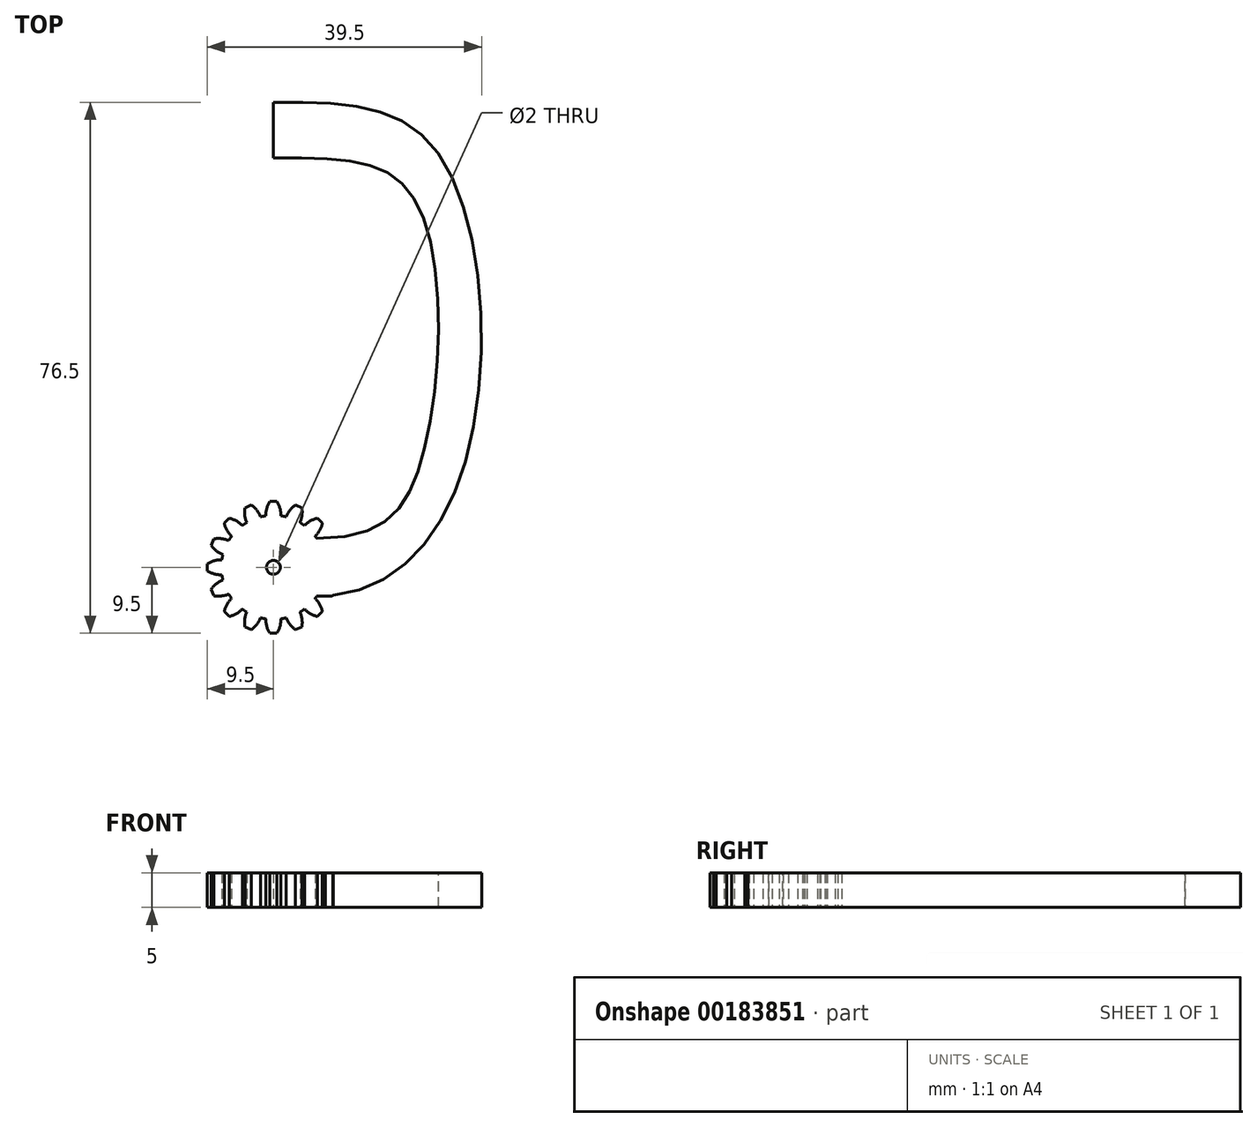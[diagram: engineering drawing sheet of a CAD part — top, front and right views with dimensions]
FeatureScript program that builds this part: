
annotation { "Feature Type Name" : "Feature", "Feature Type Description" : "" }
export const myFeature = defineFeature(function(context is Context, id is Id, definition is map)
    precondition{}
    {
        {
            var Q0;
            Q0=qCreatedBy(makeId("Top.planeOp"),FACE);
            var sketch = newSketch(context, id + "F0", { "sketchPlane" : qUnion([Q0])});
            skCircle(sketch, "E0", {"center": v(0, 0) * mm, "radius": 7.5 * mm});
            skLineSegment(sketch, "E1", {"start": v(0, 0) * mm, "end": v(0, 7.5) * mm, "construction": true});
            skLineSegment(sketch, "E2", {"start": v(0, 7.5) * mm, "end": v(0, 9.5) * mm});
            skLineSegment(sketch, "E3", {"start": v(0, 9.5) * mm, "end": v(-0.5, 9.5) * mm});
            skArc(sketch, "E4", {"start": v(-0.5, 9.5) * mm, "mid": v(-0.95, 8.5) * mm, "end": v(-1.09, 7.42) * mm});
            skLineSegment(sketch, "E5.MirrorCS", {"start": v(0, 9.5) * mm, "end": v(0.5, 9.5) * mm});
            skArc(sketch, "E6.MirrorCS", {"start": v(0.5, 9.5) * mm, "mid": v(0.95, 8.5) * mm, "end": v(1.09, 7.42) * mm});
            skArc(sketch, "E7.1.0", {"start": v(-4.1, 8.59) * mm, "mid": v(-4.13, 7.5) * mm, "end": v(-3.85, 6.44) * mm});
            skLineSegment(sketch, "E7.1.1", {"start": v(-3.64, 8.78) * mm, "end": v(-4.1, 8.59) * mm});
            skLineSegment(sketch, "E7.1.2", {"start": v(-3.64, 8.78) * mm, "end": v(-3.17, 8.97) * mm});
            skArc(sketch, "E7.1.3", {"start": v(-3.17, 8.97) * mm, "mid": v(-2.38, 8.22) * mm, "end": v(-1.83, 7.27) * mm});
            skArc(sketch, "E7.2.0", {"start": v(-7.07, 6.36) * mm, "mid": v(-6.69, 5.34) * mm, "end": v(-6.02, 4.48) * mm});
            skLineSegment(sketch, "E7.2.1", {"start": v(-6.72, 6.72) * mm, "end": v(-7.07, 6.36) * mm});
            skLineSegment(sketch, "E7.2.2", {"start": v(-6.72, 6.72) * mm, "end": v(-6.36, 7.07) * mm});
            skArc(sketch, "E7.2.3", {"start": v(-6.36, 7.07) * mm, "mid": v(-5.34, 6.69) * mm, "end": v(-4.48, 6.02) * mm});
            skArc(sketch, "E7.3.0", {"start": v(-8.97, 3.17) * mm, "mid": v(-8.22, 2.38) * mm, "end": v(-7.27, 1.83) * mm});
            skLineSegment(sketch, "E7.3.1", {"start": v(-8.78, 3.64) * mm, "end": v(-8.97, 3.17) * mm});
            skLineSegment(sketch, "E7.3.2", {"start": v(-8.78, 3.64) * mm, "end": v(-8.59, 4.1) * mm});
            skArc(sketch, "E7.3.3", {"start": v(-8.59, 4.1) * mm, "mid": v(-7.5, 4.13) * mm, "end": v(-6.44, 3.85) * mm});
            skArc(sketch, "E7.4.0", {"start": v(-9.5, -0.5) * mm, "mid": v(-8.5, -0.95) * mm, "end": v(-7.42, -1.09) * mm});
            skLineSegment(sketch, "E7.4.1", {"start": v(-9.5, 0) * mm, "end": v(-9.5, -0.5) * mm});
            skLineSegment(sketch, "E7.4.2", {"start": v(-9.5, 0) * mm, "end": v(-9.5, 0.5) * mm});
            skArc(sketch, "E7.4.3", {"start": v(-9.5, 0.5) * mm, "mid": v(-8.5, 0.95) * mm, "end": v(-7.42, 1.09) * mm});
            skArc(sketch, "E7.5.0", {"start": v(-8.59, -4.1) * mm, "mid": v(-7.5, -4.13) * mm, "end": v(-6.44, -3.85) * mm});
            skLineSegment(sketch, "E7.5.1", {"start": v(-8.78, -3.64) * mm, "end": v(-8.59, -4.1) * mm});
            skLineSegment(sketch, "E7.5.2", {"start": v(-8.78, -3.64) * mm, "end": v(-8.97, -3.17) * mm});
            skArc(sketch, "E7.5.3", {"start": v(-8.97, -3.17) * mm, "mid": v(-8.22, -2.38) * mm, "end": v(-7.27, -1.83) * mm});
            skArc(sketch, "E7.6.0", {"start": v(-6.36, -7.07) * mm, "mid": v(-5.34, -6.69) * mm, "end": v(-4.48, -6.02) * mm});
            skLineSegment(sketch, "E7.6.1", {"start": v(-6.72, -6.72) * mm, "end": v(-6.36, -7.07) * mm});
            skLineSegment(sketch, "E7.6.2", {"start": v(-6.72, -6.72) * mm, "end": v(-7.07, -6.36) * mm});
            skArc(sketch, "E7.6.3", {"start": v(-7.07, -6.36) * mm, "mid": v(-6.69, -5.34) * mm, "end": v(-6.02, -4.48) * mm});
            skArc(sketch, "E7.7.0", {"start": v(-3.17, -8.97) * mm, "mid": v(-2.38, -8.22) * mm, "end": v(-1.83, -7.27) * mm});
            skLineSegment(sketch, "E7.7.1", {"start": v(-3.64, -8.78) * mm, "end": v(-3.17, -8.97) * mm});
            skLineSegment(sketch, "E7.7.2", {"start": v(-3.64, -8.78) * mm, "end": v(-4.1, -8.59) * mm});
            skArc(sketch, "E7.7.3", {"start": v(-4.1, -8.59) * mm, "mid": v(-4.13, -7.5) * mm, "end": v(-3.85, -6.44) * mm});
            skArc(sketch, "E7.8.0", {"start": v(0.5, -9.5) * mm, "mid": v(0.95, -8.5) * mm, "end": v(1.09, -7.42) * mm});
            skLineSegment(sketch, "E7.8.1", {"start": v(0, -9.5) * mm, "end": v(0.5, -9.5) * mm});
            skLineSegment(sketch, "E7.8.2", {"start": v(0, -9.5) * mm, "end": v(-0.5, -9.5) * mm});
            skArc(sketch, "E7.8.3", {"start": v(-0.5, -9.5) * mm, "mid": v(-0.95, -8.5) * mm, "end": v(-1.09, -7.42) * mm});
            skArc(sketch, "E7.9.0", {"start": v(4.1, -8.59) * mm, "mid": v(4.13, -7.5) * mm, "end": v(3.85, -6.44) * mm});
            skLineSegment(sketch, "E7.9.1", {"start": v(3.64, -8.78) * mm, "end": v(4.1, -8.59) * mm});
            skLineSegment(sketch, "E7.9.2", {"start": v(3.64, -8.78) * mm, "end": v(3.17, -8.97) * mm});
            skArc(sketch, "E7.9.3", {"start": v(3.17, -8.97) * mm, "mid": v(2.38, -8.22) * mm, "end": v(1.83, -7.27) * mm});
            skArc(sketch, "E7.10.0", {"start": v(7.07, -6.36) * mm, "mid": v(6.69, -5.34) * mm, "end": v(6.02, -4.48) * mm});
            skLineSegment(sketch, "E7.10.1", {"start": v(6.72, -6.72) * mm, "end": v(7.07, -6.36) * mm});
            skLineSegment(sketch, "E7.10.2", {"start": v(6.72, -6.72) * mm, "end": v(6.36, -7.07) * mm});
            skArc(sketch, "E7.10.3", {"start": v(6.36, -7.07) * mm, "mid": v(5.34, -6.69) * mm, "end": v(4.48, -6.02) * mm});
            skArc(sketch, "E7.11.0", {"start": v(8.97, -3.17) * mm, "mid": v(8.22, -2.38) * mm, "end": v(7.27, -1.83) * mm});
            skLineSegment(sketch, "E7.11.1", {"start": v(8.78, -3.64) * mm, "end": v(8.97, -3.17) * mm});
            skLineSegment(sketch, "E7.11.2", {"start": v(8.78, -3.64) * mm, "end": v(8.59, -4.1) * mm});
            skArc(sketch, "E7.11.3", {"start": v(8.59, -4.1) * mm, "mid": v(7.5, -4.13) * mm, "end": v(6.44, -3.85) * mm});
            skArc(sketch, "E7.12.0", {"start": v(9.5, 0.5) * mm, "mid": v(8.5, 0.95) * mm, "end": v(7.42, 1.09) * mm});
            skLineSegment(sketch, "E7.12.1", {"start": v(9.5, 0) * mm, "end": v(9.5, 0.5) * mm});
            skLineSegment(sketch, "E7.12.2", {"start": v(9.5, 0) * mm, "end": v(9.5, -0.5) * mm});
            skArc(sketch, "E7.12.3", {"start": v(9.5, -0.5) * mm, "mid": v(8.5, -0.95) * mm, "end": v(7.42, -1.09) * mm});
            skArc(sketch, "E7.13.0", {"start": v(8.59, 4.1) * mm, "mid": v(7.5, 4.13) * mm, "end": v(6.44, 3.85) * mm});
            skLineSegment(sketch, "E7.13.1", {"start": v(8.78, 3.64) * mm, "end": v(8.59, 4.1) * mm});
            skLineSegment(sketch, "E7.13.2", {"start": v(8.78, 3.64) * mm, "end": v(8.97, 3.17) * mm});
            skArc(sketch, "E7.13.3", {"start": v(8.97, 3.17) * mm, "mid": v(8.22, 2.38) * mm, "end": v(7.27, 1.83) * mm});
            skArc(sketch, "E7.14.0", {"start": v(6.36, 7.07) * mm, "mid": v(5.34, 6.69) * mm, "end": v(4.48, 6.02) * mm});
            skLineSegment(sketch, "E7.14.1", {"start": v(6.72, 6.72) * mm, "end": v(6.36, 7.07) * mm});
            skLineSegment(sketch, "E7.14.2", {"start": v(6.72, 6.72) * mm, "end": v(7.07, 6.36) * mm});
            skArc(sketch, "E7.14.3", {"start": v(7.07, 6.36) * mm, "mid": v(6.69, 5.34) * mm, "end": v(6.02, 4.48) * mm});
            skArc(sketch, "E7.15.0", {"start": v(3.17, 8.97) * mm, "mid": v(2.38, 8.22) * mm, "end": v(1.83, 7.27) * mm});
            skLineSegment(sketch, "E7.15.1", {"start": v(3.64, 8.78) * mm, "end": v(3.17, 8.97) * mm});
            skLineSegment(sketch, "E7.15.2", {"start": v(3.64, 8.78) * mm, "end": v(4.1, 8.59) * mm});
            skArc(sketch, "E7.15.3", {"start": v(4.1, 8.59) * mm, "mid": v(4.13, 7.5) * mm, "end": v(3.85, 6.44) * mm});
            skSolve(sketch);
        }
        {
            var Q0;
            {var subQ0=sQuery(id+"F0.wireOp",EDGE,"E0");var subQ27=makeQuery(id+"F0.imprint","INTERSECT",VERTEX,{"derivedFrom":[subQ0,sQuery(id+"F0.wireOp",EDGE,"E7.12.0")]});Q0=makeQuery(id+"F0.imprint","IMPRINT",FACE,{"disambiguationData":[TD([[makeQuery(id+"F0.imprint","IMPRINT",EDGE,{"disambiguationData":[TD([[subQ27,-1.0]])],"derivedFrom":subQ0}),1.0]])]});}
            var Q1;
            {var subQ0=sQuery(id+"F0.wireOp",EDGE,"E7.8.0");Q1=makeQuery(id+"F0.imprint","IMPRINT",FACE,{"disambiguationData":[TD([[makeQuery(id+"F0.imprint","IMPRINT",EDGE,{"derivedFrom":subQ0}),1.0]])]});}
            var Q2;
            {var subQ0=sQuery(id+"F0.wireOp",EDGE,"E7.9.0");Q2=makeQuery(id+"F0.imprint","IMPRINT",FACE,{"disambiguationData":[TD([[makeQuery(id+"F0.imprint","IMPRINT",EDGE,{"derivedFrom":subQ0}),1.0]])]});}
            var Q3;
            {var subQ0=sQuery(id+"F0.wireOp",EDGE,"E7.11.0");Q3=makeQuery(id+"F0.imprint","IMPRINT",FACE,{"disambiguationData":[TD([[makeQuery(id+"F0.imprint","IMPRINT",EDGE,{"derivedFrom":subQ0}),1.0]])]});}
            var Q4;
            {var subQ0=sQuery(id+"F0.wireOp",EDGE,"E7.12.0");Q4=makeQuery(id+"F0.imprint","IMPRINT",FACE,{"disambiguationData":[TD([[makeQuery(id+"F0.imprint","IMPRINT",EDGE,{"derivedFrom":subQ0}),1.0]])]});}
            var Q5;
            {var subQ0=sQuery(id+"F0.wireOp",EDGE,"E7.10.0");Q5=makeQuery(id+"F0.imprint","IMPRINT",FACE,{"disambiguationData":[TD([[makeQuery(id+"F0.imprint","IMPRINT",EDGE,{"derivedFrom":subQ0}),1.0]])]});}
            var Q6;
            {var subQ0=sQuery(id+"F0.wireOp",EDGE,"E7.13.0");Q6=makeQuery(id+"F0.imprint","IMPRINT",FACE,{"disambiguationData":[TD([[makeQuery(id+"F0.imprint","IMPRINT",EDGE,{"derivedFrom":subQ0}),1.0]])]});}
            var Q7;
            {var subQ0=sQuery(id+"F0.wireOp",EDGE,"E7.14.0");Q7=makeQuery(id+"F0.imprint","IMPRINT",FACE,{"disambiguationData":[TD([[makeQuery(id+"F0.imprint","IMPRINT",EDGE,{"derivedFrom":subQ0}),1.0]])]});}
            var Q8;
            {var subQ0=sQuery(id+"F0.wireOp",EDGE,"E7.15.0");Q8=makeQuery(id+"F0.imprint","IMPRINT",FACE,{"disambiguationData":[TD([[makeQuery(id+"F0.imprint","IMPRINT",EDGE,{"derivedFrom":subQ0}),1.0]])]});}
            var Q9;
            {var subQ0=sQuery(id+"F0.wireOp",EDGE,"E7.7.0");Q9=makeQuery(id+"F0.imprint","IMPRINT",FACE,{"disambiguationData":[TD([[makeQuery(id+"F0.imprint","IMPRINT",EDGE,{"derivedFrom":subQ0}),1.0]])]});}
            var Q10;
            {var subQ0=sQuery(id+"F0.wireOp",EDGE,"E7.6.0");Q10=makeQuery(id+"F0.imprint","IMPRINT",FACE,{"disambiguationData":[TD([[makeQuery(id+"F0.imprint","IMPRINT",EDGE,{"derivedFrom":subQ0}),1.0]])]});}
            var Q11;
            {var subQ0=sQuery(id+"F0.wireOp",EDGE,"E7.5.0");Q11=makeQuery(id+"F0.imprint","IMPRINT",FACE,{"disambiguationData":[TD([[makeQuery(id+"F0.imprint","IMPRINT",EDGE,{"derivedFrom":subQ0}),1.0]])]});}
            var Q12;
            {var subQ1=sQuery(id+"F0.wireOp",EDGE,"E7.4.0");Q12=makeQuery(id+"F0.imprint","IMPRINT",FACE,{"disambiguationData":[TD([[makeQuery(id+"F0.imprint","IMPRINT",EDGE,{"derivedFrom":subQ1}),1.0]])]});}
            var Q13;
            {var subQ0=sQuery(id+"F0.wireOp",EDGE,"E7.3.0");Q13=makeQuery(id+"F0.imprint","IMPRINT",FACE,{"disambiguationData":[TD([[makeQuery(id+"F0.imprint","IMPRINT",EDGE,{"derivedFrom":subQ0}),1.0]])]});}
            var Q14;
            {var subQ0=sQuery(id+"F0.wireOp",EDGE,"E7.2.0");Q14=makeQuery(id+"F0.imprint","IMPRINT",FACE,{"disambiguationData":[TD([[makeQuery(id+"F0.imprint","IMPRINT",EDGE,{"derivedFrom":subQ0}),1.0]])]});}
            var Q15;
            {var subQ0=sQuery(id+"F0.wireOp",EDGE,"E7.1.0");Q15=makeQuery(id+"F0.imprint","IMPRINT",FACE,{"disambiguationData":[TD([[makeQuery(id+"F0.imprint","IMPRINT",EDGE,{"derivedFrom":subQ0}),1.0]])]});}
            var Q16;
            {var subQ0=sQuery(id+"F0.wireOp",EDGE,"E2");Q16=makeQuery(id+"F0.imprint","IMPRINT",FACE,{"disambiguationData":[TD([[makeQuery(id+"F0.imprint","IMPRINT",EDGE,{"derivedFrom":subQ0}),1.0]])]});}
            var Q17;
            {var subQ0=sQuery(id+"F0.wireOp",EDGE,"E2");Q17=makeQuery(id+"F0.imprint","IMPRINT",FACE,{"disambiguationData":[TD([[makeQuery(id+"F0.imprint","IMPRINT",EDGE,{"derivedFrom":subQ0}),-1.0]])]});}
            extrude(context, id + "F1", {"entities" : qUnion([Q0, Q1, Q2, Q3, Q4, Q5, Q6, Q7, Q8, Q9, Q10, Q11, Q12, Q13, Q14, Q15, Q16, Q17]), "depth" : 5 * mm});
        }
        {
            var Q0;
            Q0=makeQuery(id+"F1.opExtrude","CAP_FACE",FACE,{"disambiguationData":[OSD([sQuery(id+"F0.wireOp",EDGE,"E0"),sQuery(id+"F0.wireOp",EDGE,"E3"),sQuery(id+"F0.wireOp",EDGE,"E4"),sQuery(id+"F0.wireOp",EDGE,"E5.MirrorCS"),sQuery(id+"F0.wireOp",EDGE,"E6.MirrorCS"),sQuery(id+"F0.wireOp",EDGE,"E7.1.0"),sQuery(id+"F0.wireOp",EDGE,"E7.1.1"),sQuery(id+"F0.wireOp",EDGE,"E7.1.2"),sQuery(id+"F0.wireOp",EDGE,"E7.1.3"),sQuery(id+"F0.wireOp",EDGE,"E7.2.0"),sQuery(id+"F0.wireOp",EDGE,"E7.2.1"),sQuery(id+"F0.wireOp",EDGE,"E7.2.2"),sQuery(id+"F0.wireOp",EDGE,"E7.2.3"),sQuery(id+"F0.wireOp",EDGE,"E7.3.0"),sQuery(id+"F0.wireOp",EDGE,"E7.3.1"),sQuery(id+"F0.wireOp",EDGE,"E7.3.2"),sQuery(id+"F0.wireOp",EDGE,"E7.3.3"),sQuery(id+"F0.wireOp",EDGE,"E7.4.0"),sQuery(id+"F0.wireOp",EDGE,"E7.4.1"),sQuery(id+"F0.wireOp",EDGE,"E7.4.2"),sQuery(id+"F0.wireOp",EDGE,"E7.4.3"),sQuery(id+"F0.wireOp",EDGE,"E7.5.0"),sQuery(id+"F0.wireOp",EDGE,"E7.5.1"),sQuery(id+"F0.wireOp",EDGE,"E7.5.2"),sQuery(id+"F0.wireOp",EDGE,"E7.5.3"),sQuery(id+"F0.wireOp",EDGE,"E7.6.0"),sQuery(id+"F0.wireOp",EDGE,"E7.6.1"),sQuery(id+"F0.wireOp",EDGE,"E7.6.2"),sQuery(id+"F0.wireOp",EDGE,"E7.6.3"),sQuery(id+"F0.wireOp",EDGE,"E7.7.0"),sQuery(id+"F0.wireOp",EDGE,"E7.7.1"),sQuery(id+"F0.wireOp",EDGE,"E7.7.2"),sQuery(id+"F0.wireOp",EDGE,"E7.7.3"),sQuery(id+"F0.wireOp",EDGE,"E7.8.0"),sQuery(id+"F0.wireOp",EDGE,"E7.8.1"),sQuery(id+"F0.wireOp",EDGE,"E7.8.2"),sQuery(id+"F0.wireOp",EDGE,"E7.8.3"),sQuery(id+"F0.wireOp",EDGE,"E7.9.0"),sQuery(id+"F0.wireOp",EDGE,"E7.9.1"),sQuery(id+"F0.wireOp",EDGE,"E7.9.2"),sQuery(id+"F0.wireOp",EDGE,"E7.9.3"),sQuery(id+"F0.wireOp",EDGE,"E7.10.0"),sQuery(id+"F0.wireOp",EDGE,"E7.10.1"),sQuery(id+"F0.wireOp",EDGE,"E7.10.2"),sQuery(id+"F0.wireOp",EDGE,"E7.10.3"),sQuery(id+"F0.wireOp",EDGE,"E7.11.0"),sQuery(id+"F0.wireOp",EDGE,"E7.11.1"),sQuery(id+"F0.wireOp",EDGE,"E7.11.2"),sQuery(id+"F0.wireOp",EDGE,"E7.11.3"),sQuery(id+"F0.wireOp",EDGE,"E7.12.0"),sQuery(id+"F0.wireOp",EDGE,"E7.12.1"),sQuery(id+"F0.wireOp",EDGE,"E7.12.2"),sQuery(id+"F0.wireOp",EDGE,"E7.12.3"),sQuery(id+"F0.wireOp",EDGE,"E7.13.0"),sQuery(id+"F0.wireOp",EDGE,"E7.13.1"),sQuery(id+"F0.wireOp",EDGE,"E7.13.2"),sQuery(id+"F0.wireOp",EDGE,"E7.13.3"),sQuery(id+"F0.wireOp",EDGE,"E7.14.0"),sQuery(id+"F0.wireOp",EDGE,"E7.14.1"),sQuery(id+"F0.wireOp",EDGE,"E7.14.2"),sQuery(id+"F0.wireOp",EDGE,"E7.14.3"),sQuery(id+"F0.wireOp",EDGE,"E7.15.0"),sQuery(id+"F0.wireOp",EDGE,"E7.15.1"),sQuery(id+"F0.wireOp",EDGE,"E7.15.2"),sQuery(id+"F0.wireOp",EDGE,"E7.15.3")])],"isStart":false});
            var sketch = newSketch(context, id + "F2", { "sketchPlane" : qUnion([Q0])});
            skCircle(sketch, "E8", {"center": v(0, 0) * mm, "radius": 1 * mm});
            skSolve(sketch);
        }
        {
            var Q0;
            Q0=makeQuery(id+"F2.imprint","IMPRINT",FACE,{"disambiguationData":[TD([[makeQuery(id+"F2.imprint","IMPRINT",EDGE,{"derivedFrom":sQuery(id+"F2.wireOp",EDGE,"E8")}),1.0]])]});
            extrude(context, id + "F3", {"entities" : qUnion([Q0]), "operationType" : NewBodyOperationType.REMOVE, "oppositeDirection" : true, "depth" : 5 * mm});
        }
        {
            var Q0;
            Q0=qCreatedBy(makeId("Top.planeOp"),FACE);
            var sketch = newSketch(context, id + "F4", { "sketchPlane" : qUnion([Q0])});
            skLineSegment(sketch, "E9", {"start": v(0, 59) * mm, "end": v(0, 67) * mm});
            skFitSpline(sketch, "E10", {"points": [v(0, 59) * mm, v(20.27, 53.12) * mm, v(21.57, 16.26) * mm, v(6.24, 4.17) * mm], "startDerivative": vector(98.5, 0) * mm, "endDerivative": vector(-102.42, 0) * mm});
            skFitSpline(sketch, "E11", {"points": [v(0, 67) * mm, v(23.38, 60.13) * mm, v(27.25, 13.83) * mm, v(6.24, -4.17) * mm], "startDerivative": vector(103.38, 0) * mm, "endDerivative": vector(-97.04, 0) * mm});
            skLineSegment(sketch, "E12", {"start": v(6.24, -4.17) * mm, "end": v(6.24, 4.17) * mm});
            skSolve(sketch);
        }
        {
            var Q0;
            Q0 = qSketchRegion(id + "F4", true);
            var Q1;
            Q1=makeQuery(id+"F1.opExtrude","CAP_FACE",FACE,{"disambiguationData":[OSD([sQuery(id+"F0.wireOp",EDGE,"E0"),sQuery(id+"F0.wireOp",EDGE,"E3"),sQuery(id+"F0.wireOp",EDGE,"E4"),sQuery(id+"F0.wireOp",EDGE,"E5.MirrorCS"),sQuery(id+"F0.wireOp",EDGE,"E6.MirrorCS"),sQuery(id+"F0.wireOp",EDGE,"E7.1.0"),sQuery(id+"F0.wireOp",EDGE,"E7.1.1"),sQuery(id+"F0.wireOp",EDGE,"E7.1.2"),sQuery(id+"F0.wireOp",EDGE,"E7.1.3"),sQuery(id+"F0.wireOp",EDGE,"E7.2.0"),sQuery(id+"F0.wireOp",EDGE,"E7.2.1"),sQuery(id+"F0.wireOp",EDGE,"E7.2.2"),sQuery(id+"F0.wireOp",EDGE,"E7.2.3"),sQuery(id+"F0.wireOp",EDGE,"E7.3.0"),sQuery(id+"F0.wireOp",EDGE,"E7.3.1"),sQuery(id+"F0.wireOp",EDGE,"E7.3.2"),sQuery(id+"F0.wireOp",EDGE,"E7.3.3"),sQuery(id+"F0.wireOp",EDGE,"E7.4.0"),sQuery(id+"F0.wireOp",EDGE,"E7.4.1"),sQuery(id+"F0.wireOp",EDGE,"E7.4.2"),sQuery(id+"F0.wireOp",EDGE,"E7.4.3"),sQuery(id+"F0.wireOp",EDGE,"E7.5.0"),sQuery(id+"F0.wireOp",EDGE,"E7.5.1"),sQuery(id+"F0.wireOp",EDGE,"E7.5.2"),sQuery(id+"F0.wireOp",EDGE,"E7.5.3"),sQuery(id+"F0.wireOp",EDGE,"E7.6.0"),sQuery(id+"F0.wireOp",EDGE,"E7.6.1"),sQuery(id+"F0.wireOp",EDGE,"E7.6.2"),sQuery(id+"F0.wireOp",EDGE,"E7.6.3"),sQuery(id+"F0.wireOp",EDGE,"E7.7.0"),sQuery(id+"F0.wireOp",EDGE,"E7.7.1"),sQuery(id+"F0.wireOp",EDGE,"E7.7.2"),sQuery(id+"F0.wireOp",EDGE,"E7.7.3"),sQuery(id+"F0.wireOp",EDGE,"E7.8.0"),sQuery(id+"F0.wireOp",EDGE,"E7.8.1"),sQuery(id+"F0.wireOp",EDGE,"E7.8.2"),sQuery(id+"F0.wireOp",EDGE,"E7.8.3"),sQuery(id+"F0.wireOp",EDGE,"E7.9.0"),sQuery(id+"F0.wireOp",EDGE,"E7.9.1"),sQuery(id+"F0.wireOp",EDGE,"E7.9.2"),sQuery(id+"F0.wireOp",EDGE,"E7.9.3"),sQuery(id+"F0.wireOp",EDGE,"E7.10.0"),sQuery(id+"F0.wireOp",EDGE,"E7.10.1"),sQuery(id+"F0.wireOp",EDGE,"E7.10.2"),sQuery(id+"F0.wireOp",EDGE,"E7.10.3"),sQuery(id+"F0.wireOp",EDGE,"E7.11.0"),sQuery(id+"F0.wireOp",EDGE,"E7.11.1"),sQuery(id+"F0.wireOp",EDGE,"E7.11.2"),sQuery(id+"F0.wireOp",EDGE,"E7.11.3"),sQuery(id+"F0.wireOp",EDGE,"E7.12.0"),sQuery(id+"F0.wireOp",EDGE,"E7.12.1"),sQuery(id+"F0.wireOp",EDGE,"E7.12.2"),sQuery(id+"F0.wireOp",EDGE,"E7.12.3"),sQuery(id+"F0.wireOp",EDGE,"E7.13.0"),sQuery(id+"F0.wireOp",EDGE,"E7.13.1"),sQuery(id+"F0.wireOp",EDGE,"E7.13.2"),sQuery(id+"F0.wireOp",EDGE,"E7.13.3"),sQuery(id+"F0.wireOp",EDGE,"E7.14.0"),sQuery(id+"F0.wireOp",EDGE,"E7.14.1"),sQuery(id+"F0.wireOp",EDGE,"E7.14.2"),sQuery(id+"F0.wireOp",EDGE,"E7.14.3"),sQuery(id+"F0.wireOp",EDGE,"E7.15.0"),sQuery(id+"F0.wireOp",EDGE,"E7.15.1"),sQuery(id+"F0.wireOp",EDGE,"E7.15.2"),sQuery(id+"F0.wireOp",EDGE,"E7.15.3")])],"isStart":false});
            extrude(context, id + "F5", {"entities" : qUnion([Q0]), "operationType" : NewBodyOperationType.ADD, "endBound" : BoundingType.UP_TO_SURFACE, "endBoundEntityFace" : qUnion([Q1]), "depth" : 25 * mm});
        }
    });
